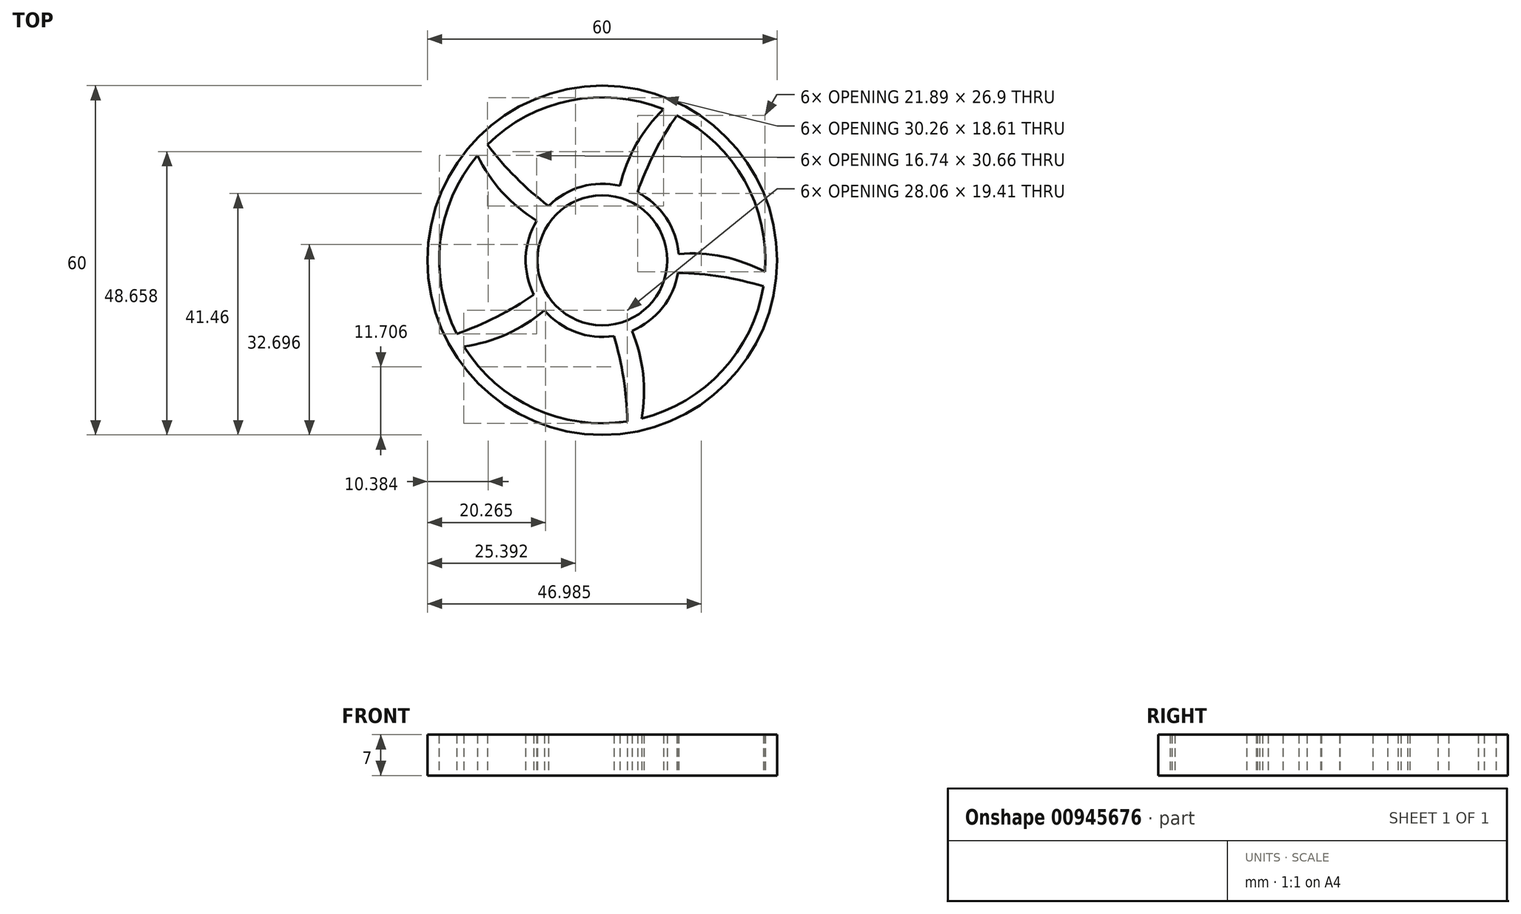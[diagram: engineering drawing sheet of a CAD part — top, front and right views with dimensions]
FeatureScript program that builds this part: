
annotation { "Feature Type Name" : "Feature", "Feature Type Description" : "" }
export const myFeature = defineFeature(function(context is Context, id is Id, definition is map)
    precondition{}
    {
        {
            var Q0;
            Q0=qCreatedBy(makeId("Top.planeOp"),FACE);
            var sketch = newSketch(context, id + "F0", { "sketchPlane" : qUnion([Q0])});
            skCircle(sketch, "E0", {"center": v(0, 0) * mm, "radius": 11.15 * mm});
            skCircle(sketch, "E1.0", {"center": v(0, 0) * mm, "radius": 13.15 * mm});
            skArc(sketch, "E2", {"start": v(-21.43, 18.03) * mm, "mid": v(-17.14, 11.69) * mm, "end": v(-11.25, 6.82) * mm});
            skArc(sketch, "E3", {"start": v(-19.74, 19.86) * mm, "mid": v(-14.85, 14.25) * mm, "end": v(-9.24, 9.35) * mm});
            skCircle(sketch, "E4", {"center": v(0, 0) * mm, "radius": 28 * mm});
            skCircle(sketch, "E5.0", {"center": v(0, 0) * mm, "radius": 30 * mm});
            skArc(sketch, "E6.1.0", {"start": v(-24.99, -12.63) * mm, "mid": v(-18.14, -9.72) * mm, "end": v(-11.75, -5.9) * mm});
            skArc(sketch, "E6.1.1", {"start": v(-23.76, -14.8) * mm, "mid": v(-16.41, -12.7) * mm, "end": v(-9.96, -8.59) * mm});
            skArc(sketch, "E6.2.0", {"start": v(4.3, -27.67) * mm, "mid": v(3.63, -20.26) * mm, "end": v(1.98, -13) * mm});
            skArc(sketch, "E6.2.1", {"start": v(6.74, -27.18) * mm, "mid": v(7, -19.53) * mm, "end": v(5.1, -12.12) * mm});
            skArc(sketch, "E6.3.0", {"start": v(27.64, -4.47) * mm, "mid": v(20.39, -2.8) * mm, "end": v(12.98, -2.13) * mm});
            skArc(sketch, "E6.3.1", {"start": v(27.93, -1.99) * mm, "mid": v(20.74, 0.62) * mm, "end": v(13.1, 1.1) * mm});
            skArc(sketch, "E6.4.0", {"start": v(12.79, 24.9) * mm, "mid": v(8.97, 18.52) * mm, "end": v(6.04, 11.68) * mm});
            skArc(sketch, "E6.4.1", {"start": v(10.52, 25.95) * mm, "mid": v(5.82, 19.92) * mm, "end": v(3, 12.8) * mm});
            skSolve(sketch);
        }
        {
            var Q0;
            Q0=makeQuery(id+"F0.imprint","IMPRINT",FACE,{"disambiguationData":[TD([[makeQuery(id+"F0.imprint","IMPRINT",EDGE,{"derivedFrom":sQuery(id+"F0.wireOp",EDGE,"E0")}),-1.0]])]});
            var Q1;
            {var subQ0=sQuery(id+"F0.wireOp",EDGE,"E2");Q1=makeQuery(id+"F0.imprint","IMPRINT",FACE,{"disambiguationData":[TD([[makeQuery(id+"F0.imprint","IMPRINT",EDGE,{"derivedFrom":subQ0}),1.0]])]});}
            var Q2;
            {var subQ0=sQuery(id+"F0.wireOp",EDGE,"E6.4.0");Q2=makeQuery(id+"F0.imprint","IMPRINT",FACE,{"disambiguationData":[TD([[makeQuery(id+"F0.imprint","IMPRINT",EDGE,{"derivedFrom":subQ0}),-1.0]])]});}
            var Q3;
            {var subQ0=sQuery(id+"F0.wireOp",EDGE,"E6.3.0");Q3=makeQuery(id+"F0.imprint","IMPRINT",FACE,{"disambiguationData":[TD([[makeQuery(id+"F0.imprint","IMPRINT",EDGE,{"derivedFrom":subQ0}),-1.0]])]});}
            var Q4;
            {var subQ0=sQuery(id+"F0.wireOp",EDGE,"E6.2.0");Q4=makeQuery(id+"F0.imprint","IMPRINT",FACE,{"disambiguationData":[TD([[makeQuery(id+"F0.imprint","IMPRINT",EDGE,{"derivedFrom":subQ0}),-1.0]])]});}
            var Q5;
            {var subQ0=sQuery(id+"F0.wireOp",EDGE,"E6.1.0");Q5=makeQuery(id+"F0.imprint","IMPRINT",FACE,{"disambiguationData":[TD([[makeQuery(id+"F0.imprint","IMPRINT",EDGE,{"derivedFrom":subQ0}),-1.0]])]});}
            var Q6;
            Q6=makeQuery(id+"F0.imprint","IMPRINT",FACE,{"disambiguationData":[TD([[makeQuery(id+"F0.imprint","IMPRINT",EDGE,{"derivedFrom":sQuery(id+"F0.wireOp",EDGE,"E5.0")}),1.0]])]});
            extrude(context, id + "F1", {"entities" : qUnion([Q0, Q1, Q2, Q3, Q4, Q5, Q6]), "depth" : 7 * mm, "offsetDistance" : 25 * mm});
        }
    });
